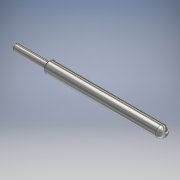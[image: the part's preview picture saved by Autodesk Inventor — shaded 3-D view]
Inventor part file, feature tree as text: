
AUTODESK INVENTOR PART (.ipt)
format: ipt  version: 2018 (Build 220112000, 112)  size: 114,688 bytes
history: native  units: mm
features: fillet x3, revolve x1, sketch x1
ambient origin geometry x8: Origin, YZ Plane, XZ Plane, XY Plane, X Axis, Y Axis, Z Axis, Center Point
bodies: Solid1 (feature_tree)
feature tree (5):
  revolve  "Revolution1"  [1 undecoded]
  fillet  "Fillet1"  Radius=6.0mm
  fillet  "Fillet2"  Radius=62.0mm
  fillet  "Fillet3"  [1 undecoded]
  sketch  "Sketch1"  dims[d0=275.0mm d1=10.0mm d2=6.0mm d3=62.0mm d5=135.0deg d6=90.0deg d7=10.0mm d8=10.0mm d9=6.0mm]
note: 2 required parameter values undecoded (feature->parameter linkage not recoverable at this tier; creation-order binding heuristic only, values carry confidence <= 0.55)